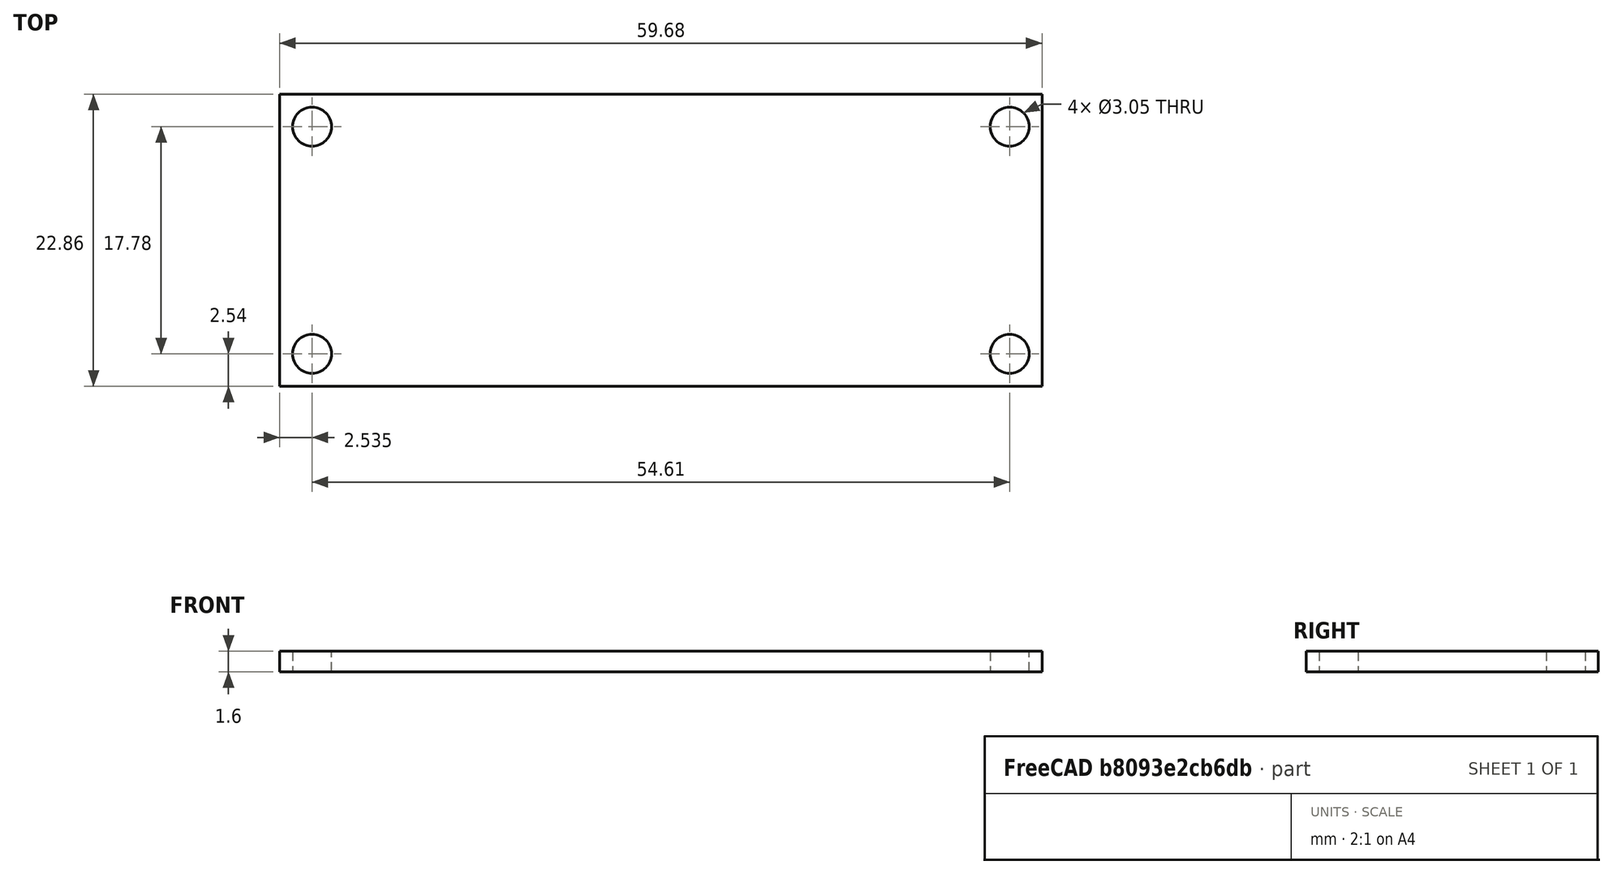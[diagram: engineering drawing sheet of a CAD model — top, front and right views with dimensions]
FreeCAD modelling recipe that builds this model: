
FCSTD DOCUMENT  (FreeCAD 0.21R33668 +26 (Git))
Label: ESP32_ThingPlus_C_Dimensional_Mounting
License: All rights reserved
LicenseURL: http://en.wikipedia.org/wiki/All_rights_reserved
objects: Sketcher::SketchObject×1, PartDesign::Pad×1, PartDesign::Body×1
note: 4 computed .brp shape members not serialized (recipe doc carries the construction recipe); baked Part::Feature solids carry a one-line shape summary decoded from their .brp

FEATURE [Sketcher::SketchObject] Sketch
  FullyConstrained = true
  MapMode = 5
  Support = -> [XY_Plane]
  sketch-geometry (8):
    g0: LineSegment StartX=-29.845 StartY=11.43 StartZ=0 EndX=29.845 EndY=11.43 EndZ=0
    g1: LineSegment StartX=29.845 StartY=11.43 StartZ=0 EndX=29.845 EndY=-11.43 EndZ=0
    g2: LineSegment StartX=29.845 StartY=-11.43 StartZ=0 EndX=-29.845 EndY=-11.43 EndZ=0
    g3: LineSegment StartX=-29.845 StartY=-11.43 StartZ=0 EndX=-29.845 EndY=11.43 EndZ=0
    g4: Circle CenterX=-27.305 CenterY=8.89 CenterZ=0 NormalX=0 NormalY=0 NormalZ=1 AngleXU=0 Radius=1.524
    g5: Circle CenterX=-27.305 CenterY=-8.89 CenterZ=0 NormalX=0 NormalY=0 NormalZ=1 AngleXU=0 Radius=1.524
    g6: Circle CenterX=27.305 CenterY=-8.89 CenterZ=0 NormalX=0 NormalY=0 NormalZ=1 AngleXU=0 Radius=1.524
    g7: Circle CenterX=27.305 CenterY=8.89 CenterZ=0 NormalX=0 NormalY=0 NormalZ=1 AngleXU=0 Radius=1.524
  constraints (21):
    c: Coincident(g0,g1)
    c: Coincident(g1,g2)
    c: Coincident(g2,g3)
    c: Coincident(g3,g0)
    c: Horizontal(g0)
    c: Horizontal(g2)
    c: Vertical(g1)
    c: Vertical(g3)
    c: DistanceY(g1,g1) = 22.86
    c: DistanceX(g0,g0) = 59.69
    c: Symmetric(g1,g0,g-1)
    c: Diameter(g4) = 3.048
    c: Equal(g4,g7)
    c: Equal(g4,g5)
    c: Equal(g4,g6)
    c: DistanceX(g4,g7) = 54.61
    c: Vertical(g7,g6)
    c: DistanceY(g5,g4) = 17.78
    c: Symmetric(g7,g4,g-2)
    c: Horizontal(g6,g5)
    c: Symmetric(g4,g5,g-1)
FEATURE [PartDesign::Pad] Pad
  Direction = (0,0,1)
  Length = 1.6
  Length2 = 10
  Profile = -> Sketch
  ReferenceAxis = -> Sketch [N_Axis]
  Type = 0
FEATURE [PartDesign::Body] Body
  Group = -> [Sketch,Pad]
  Origin = -> Origin
  Tip = -> Pad
